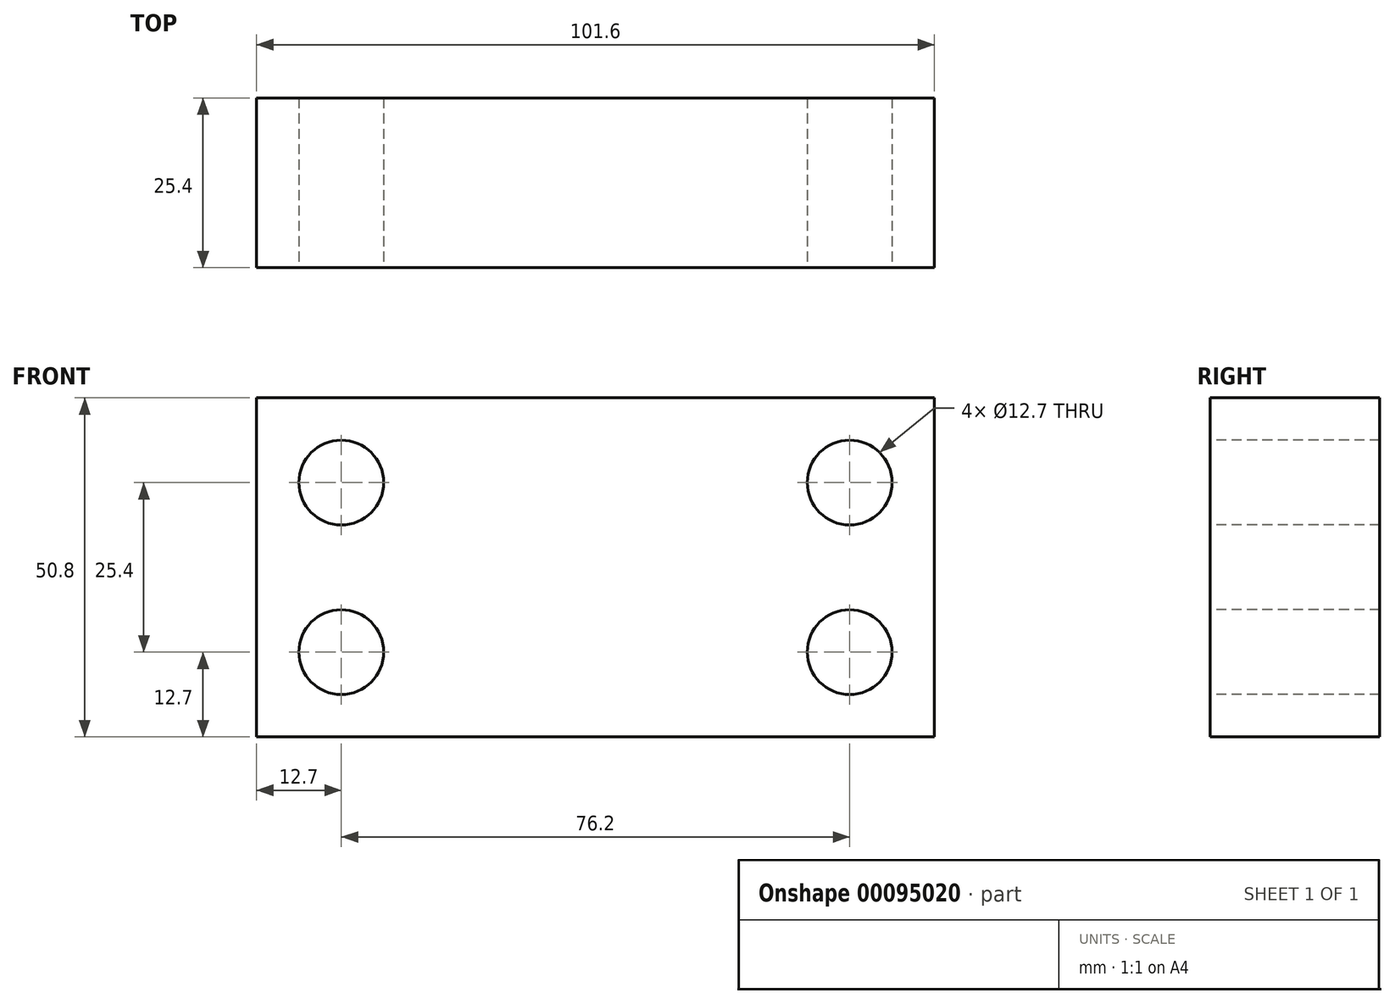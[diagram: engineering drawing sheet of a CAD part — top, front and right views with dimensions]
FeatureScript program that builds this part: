
annotation { "Feature Type Name" : "Feature", "Feature Type Description" : "" }
export const myFeature = defineFeature(function(context is Context, id is Id, definition is map)
    precondition{}
    {
        {
            var Q0;
            Q0=qCreatedBy(makeId("Front.planeOp"),FACE);
            var sketch = newSketch(context, id + "F0", { "sketchPlane" : qUnion([Q0])});
            skLineSegment(sketch, "E0.bottom", {"start": v(-50.8, -25.4) * mm, "end": v(50.8, -25.4) * mm});
            skLineSegment(sketch, "E0.top", {"start": v(-50.8, 25.4) * mm, "end": v(50.8, 25.4) * mm});
            skLineSegment(sketch, "E0.left", {"start": v(-50.8, -25.4) * mm, "end": v(-50.8, 25.4) * mm});
            skLineSegment(sketch, "E0.right", {"start": v(50.8, -25.4) * mm, "end": v(50.8, 25.4) * mm});
            skPoint(sketch, "E0.middle", {"position": v(0, 0) * mm});
            skSolve(sketch);
        }
        {
            var Q0;
            Q0 = qSketchRegion(id + "F0", true);
            extrude(context, id + "F1", {"entities" : qUnion([Q0]), "oppositeDirection" : true, "depth" : 25.4 * mm});
        }
        {
            var Q0;
            Q0=makeQuery(id+"F1.opExtrude","CAP_FACE",FACE,{"disambiguationData":[OSD([sQuery(id+"F0.wireOp",EDGE,"E0.bottom"),sQuery(id+"F0.wireOp",EDGE,"E0.top"),sQuery(id+"F0.wireOp",EDGE,"E0.left"),sQuery(id+"F0.wireOp",EDGE,"E0.right")])],"isStart":true});
            var sketch = newSketch(context, id + "F2", { "sketchPlane" : qUnion([Q0])});
            skCircle(sketch, "E1", {"center": v(-38.1, 12.7) * mm, "radius": 6.35 * mm});
            skCircle(sketch, "E2", {"center": v(-38.1, -12.7) * mm, "radius": 6.35 * mm});
            skCircle(sketch, "E3", {"center": v(38.1, 12.7) * mm, "radius": 6.35 * mm});
            skCircle(sketch, "E4", {"center": v(38.1, -12.7) * mm, "radius": 6.35 * mm});
            skSolve(sketch);
        }
        {
            var Q0;
            Q0=makeQuery(id+"F2.imprint","IMPRINT",FACE,{"disambiguationData":[TD([[makeQuery(id+"F2.imprint","IMPRINT",EDGE,{"derivedFrom":sQuery(id+"F2.wireOp",EDGE,"E1")}),1.0]])]});
            var Q1;
            Q1=makeQuery(id+"F2.imprint","IMPRINT",FACE,{"disambiguationData":[TD([[makeQuery(id+"F2.imprint","IMPRINT",EDGE,{"derivedFrom":sQuery(id+"F2.wireOp",EDGE,"E2")}),1.0]])]});
            var Q2;
            Q2=makeQuery(id+"F2.imprint","IMPRINT",FACE,{"disambiguationData":[TD([[makeQuery(id+"F2.imprint","IMPRINT",EDGE,{"derivedFrom":sQuery(id+"F2.wireOp",EDGE,"E3")}),1.0]])]});
            var Q3;
            Q3=makeQuery(id+"F2.imprint","IMPRINT",FACE,{"disambiguationData":[TD([[makeQuery(id+"F2.imprint","IMPRINT",EDGE,{"derivedFrom":sQuery(id+"F2.wireOp",EDGE,"E4")}),1.0]])]});
            extrude(context, id + "F3", {"entities" : qUnion([Q0, Q1, Q2, Q3]), "operationType" : NewBodyOperationType.REMOVE, "endBound" : BoundingType.THROUGH_ALL, "oppositeDirection" : true, "depth" : 25.4 * mm});
        }
        {
            var Q0;
            Q0=qCreatedBy(makeId("Top.planeOp"),FACE);
            var sketch = newSketch(context, id + "F4", { "sketchPlane" : qUnion([Q0])});
            skLineSegment(sketch, "E5.bottom", {"start": v(0, 50.8) * mm, "end": v(-12.7, 50.8) * mm});
            skLineSegment(sketch, "E5.top", {"start": v(0, 25.4) * mm, "end": v(-12.7, 25.4) * mm});
            skLineSegment(sketch, "E5.left", {"start": v(0, 50.8) * mm, "end": v(0, 25.4) * mm});
            skLineSegment(sketch, "E5.right", {"start": v(-12.7, 50.8) * mm, "end": v(-12.7, 25.4) * mm});
            skLineSegment(sketch, "E6.bottom", {"start": v(-6.35, 25.4) * mm, "end": v(-13.28, 25.4) * mm});
            skLineSegment(sketch, "E6.top", {"start": v(-10.65, 25.4) * mm, "end": v(-13.28, 25.4) * mm});
            skSolve(sketch);
        }
        {
            var Q0;
            Q0=qCreatedBy(makeId("Top.planeOp"),FACE);
            var sketch = newSketch(context, id + "F5", { "sketchPlane" : qUnion([Q0])});
            skLineSegment(sketch, "E7.bottom", {"start": v(5.05, 45.23) * mm, "end": v(12.67, 45.23) * mm});
            skLineSegment(sketch, "E7.top", {"start": v(5.05, 37.61) * mm, "end": v(12.67, 37.61) * mm});
            skLineSegment(sketch, "E7.left", {"start": v(5.05, 45.23) * mm, "end": v(5.05, 37.61) * mm});
            skLineSegment(sketch, "E7.right", {"start": v(12.67, 45.23) * mm, "end": v(12.67, 37.61) * mm});
            skSolve(sketch);
        }
        {
            var Q0;
            Q0=makeQuery(id+"F4.imprint","IMPRINT",FACE,{"disambiguationData":[TD([[makeQuery(id+"F4.imprint","IMPRINT",EDGE,{"derivedFrom":sQuery(id+"F4.wireOp",EDGE,"E5.bottom")}),1.0]])]});
            var Q1;
            Q1=makeQuery(id+"F5.imprint","IMPRINT",FACE,{"disambiguationData":[TD([[makeQuery(id+"F5.imprint","IMPRINT",EDGE,{"derivedFrom":sQuery(id+"F5.wireOp",EDGE,"E7.bottom")}),-1.0]])]});
            var Q2;
            Q2=sQuery(id+"F4.wireOp",EDGE,"E5.left");
            revolve(context, id + "F6", {"operationType" : NewBodyOperationType.REMOVE, "entities" : qUnion([Q0, Q1]), "axis" : qUnion([Q2]), "revolveType" : RevolveType.ONE_DIRECTION, "angle" : 30 * degree});
        }
        {
            var Q0;
            Q0=makeQuery(id+"F5.imprint","IMPRINT",FACE,{"disambiguationData":[TD([[makeQuery(id+"F5.imprint","IMPRINT",EDGE,{"derivedFrom":sQuery(id+"F5.wireOp",EDGE,"E7.bottom")}),-1.0]])]});
            var Q1;
            Q1=sQuery(id+"F4.wireOp",EDGE,"E5.left");
            revolve(context, id + "F7", {"operationType" : NewBodyOperationType.REMOVE, "entities" : qUnion([Q0]), "axis" : qUnion([Q1]), "revolveType" : RevolveType.FULL, "oppositeDirection" : true});
        }
    });
